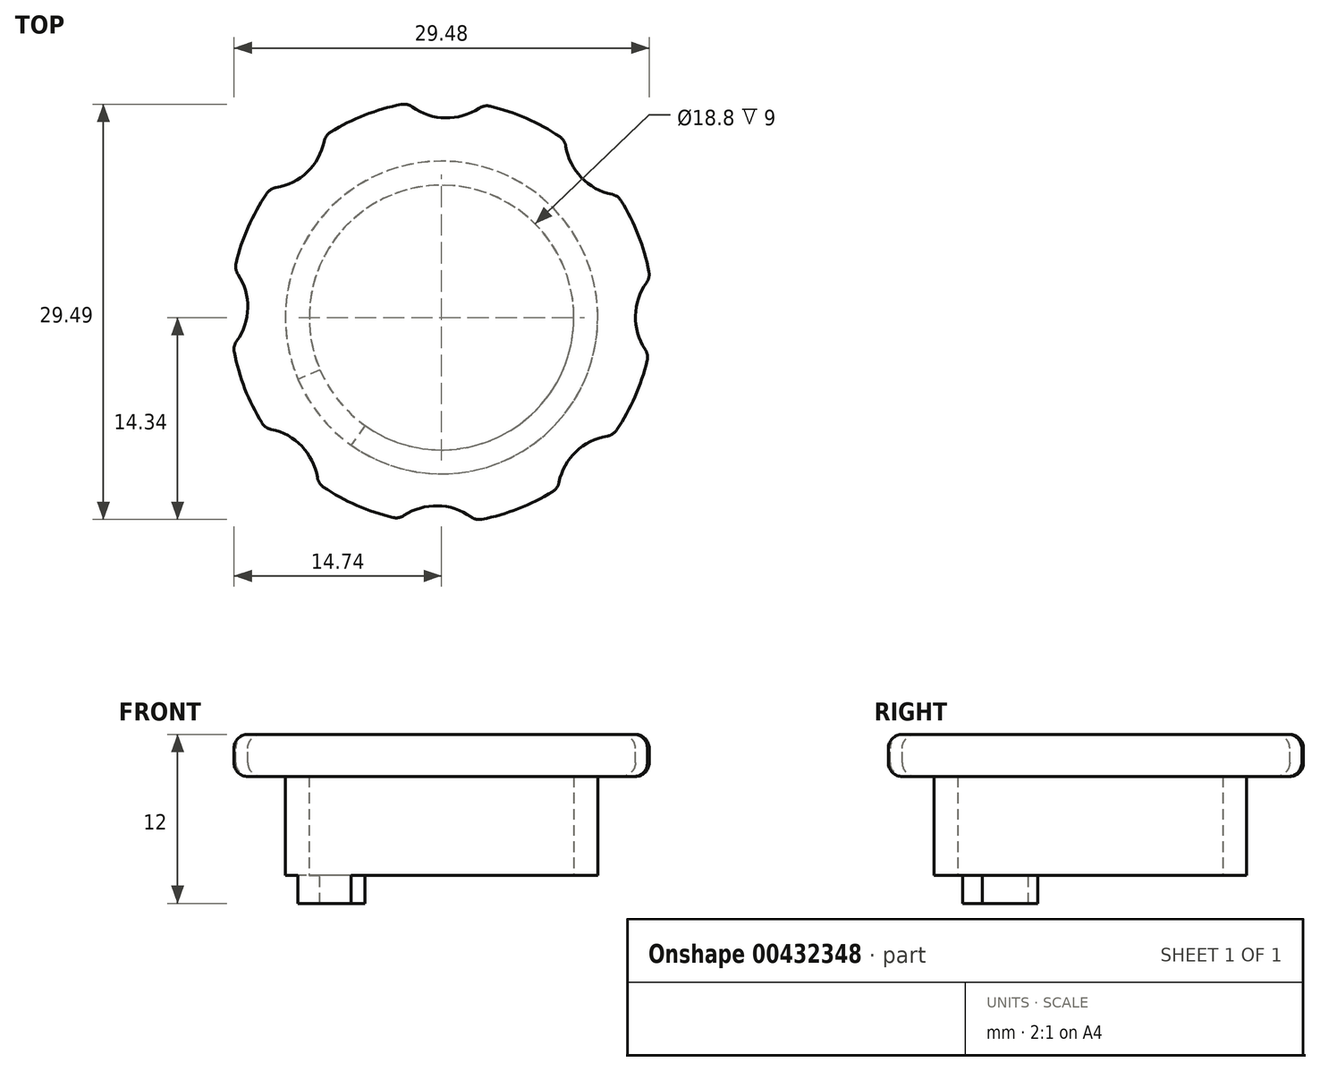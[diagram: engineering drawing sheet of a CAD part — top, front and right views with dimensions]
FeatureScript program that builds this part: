
annotation { "Feature Type Name" : "Feature", "Feature Type Description" : "" }
export const myFeature = defineFeature(function(context is Context, id is Id, definition is map)
    precondition{}
    {
        {
            var Q0;
            Q0=qCreatedBy(makeId("Top.planeOp"),FACE);
            var sketch = newSketch(context, id + "F0", { "sketchPlane" : qUnion([Q0])});
            skCircle(sketch, "E0", {"center": v(0, 0) * mm, "radius": 11.1 * mm});
            skCircle(sketch, "E1", {"center": v(0, 0) * mm, "radius": 9.4 * mm});
            skSolve(sketch);
        }
        {
            var Q0;
            Q0=makeQuery(id+"F0.imprint","IMPRINT",FACE,{"disambiguationData":[TD([[makeQuery(id+"F0.imprint","IMPRINT",EDGE,{"derivedFrom":sQuery(id+"F0.wireOp",EDGE,"E0")}),1.0]])]});
            extrude(context, id + "F1", {"entities" : qUnion([Q0]), "depth" : 10 * mm});
        }
        {
            var Q0;
            Q0=makeQuery(id+"F1.opExtrude","CAP_FACE",FACE,{"disambiguationData":[OSD([sQuery(id+"F0.wireOp",EDGE,"E0"),sQuery(id+"F0.wireOp",EDGE,"E1")])],"isStart":true});
            var sketch = newSketch(context, id + "F2", { "sketchPlane" : qUnion([Q0])});
            skLineSegment(sketch, "E2", {"start": v(-8.63, 3.72) * mm, "end": v(-10.2, 4.4) * mm});
            skLineSegment(sketch, "E3", {"start": v(-5.43, 7.67) * mm, "end": v(-6.42, 9.06) * mm});
            skArc(sketch, "E4", {"start": v(-6.42, 9.06) * mm, "mid": v(-8.63, 6.99) * mm, "end": v(-10.2, 4.4) * mm});
            skArc(sketch, "E5", {"start": v(-5.43, 7.67) * mm, "mid": v(-7.3, 5.92) * mm, "end": v(-8.63, 3.72) * mm});
            skSolve(sketch);
        }
        {
            var Q0;
            Q0=makeQuery(id+"F2.imprint","IMPRINT",FACE,{"disambiguationData":[TD([[makeQuery(id+"F2.imprint","IMPRINT",EDGE,{"derivedFrom":sQuery(id+"F2.wireOp",EDGE,"E2")}),-1.0]])]});
            extrude(context, id + "F3", {"entities" : qUnion([Q0]), "operationType" : NewBodyOperationType.ADD, "depth" : 2 * mm});
        }
        {
            var Q0;
            Q0=makeQuery(id+"F1.opExtrude","CAP_FACE",FACE,{"disambiguationData":[OSD([sQuery(id+"F0.wireOp",EDGE,"E0"),sQuery(id+"F0.wireOp",EDGE,"E1")])],"isStart":false});
            var sketch = newSketch(context, id + "F4", { "sketchPlane" : qUnion([Q0])});
            skCircle(sketch, "E6", {"center": v(0, 0.4) * mm, "radius": 15 * mm});
            skSolve(sketch);
        }
        {
            var Q0;
            Q0=makeQuery(id+"F4.imprint","IMPRINT",FACE,{"disambiguationData":[TD([[makeQuery(id+"F4.imprint","IMPRINT",EDGE,{"derivedFrom":sQuery(id+"F4.wireOp",EDGE,"E6")}),1.0]])]});
            var Q1;
            Q1=makeQuery(id+"F4.imprint","IMPRINT",FACE,{"disambiguationData":[TD([[makeQuery(id+"F4.imprint","IMPRINT",EDGE,{"derivedFrom":makeQuery(id+"F1.opExtrude","CAP_EDGE",EDGE,{"disambiguationData":[OSD([sQuery(id+"F0.wireOp",EDGE,"E0")])],"isStart":false})}),1.0]])]});
            var Q2;
            Q2=makeQuery(id+"F4.imprint","IMPRINT",FACE,{"disambiguationData":[TD([[makeQuery(id+"F4.imprint","IMPRINT",EDGE,{"derivedFrom":makeQuery(id+"F1.opExtrude","CAP_EDGE",EDGE,{"disambiguationData":[OSD([sQuery(id+"F0.wireOp",EDGE,"E1")])],"isStart":false})}),1.0]])]});
            extrude(context, id + "F5", {"entities" : qUnion([Q0, Q1, Q2]), "operationType" : NewBodyOperationType.ADD, "oppositeDirection" : true, "depth" : 3 * mm});
        }
        {
            var Q0;
            Q0=makeQuery(id+"F5.boolean.opBoolean","MERGE",FACE,{"derivedFrom":[makeQuery(id+"F1.opExtrude","CAP_FACE",FACE,{"disambiguationData":[OSD([sQuery(id+"F0.wireOp",EDGE,"E0"),sQuery(id+"F0.wireOp",EDGE,"E1")])],"isStart":false}),makeQuery(id+"F5.opExtrude","CAP_FACE",FACE,{"disambiguationData":[OSD([sQuery(id+"F4.wireOp",EDGE,"E6")])],"isStart":true})]});
            var sketch = newSketch(context, id + "F6", { "sketchPlane" : qUnion([Q0])});
            skCircle(sketch, "E7", {"center": v(0.36, 18.33) * mm, "radius": 4.17 * mm});
            skSolve(sketch);
        }
        {
            var Q0;
            {var subQ0=sQuery(id+"F6.wireOp",EDGE,"E7");var subQ1=makeQuery(id+"F5.opExtrude","CAP_EDGE",EDGE,{"disambiguationData":[OSD([sQuery(id+"F4.wireOp",EDGE,"E6")])],"isStart":true});var subQ2=makeQuery(id+"F6.imprint","INTERSECT",VERTEX,{"disambiguationData":[OD(0.0)],"derivedFrom":[subQ1,subQ0]});Q0=makeQuery(id+"F6.imprint","IMPRINT",FACE,{"disambiguationData":[TD([[makeQuery(id+"F6.imprint","IMPRINT",EDGE,{"disambiguationData":[TD([[subQ2,1.0]])],"derivedFrom":subQ0}),1.0]])]});}
            var Q1;
            {var subQ0=sQuery(id+"F6.wireOp",EDGE,"E7");var subQ1=makeQuery(id+"F5.opExtrude","CAP_EDGE",EDGE,{"disambiguationData":[OSD([sQuery(id+"F4.wireOp",EDGE,"E6")])],"isStart":true});var subQ2=makeQuery(id+"F6.imprint","INTERSECT",VERTEX,{"disambiguationData":[OD(0.0)],"derivedFrom":[subQ1,subQ0]});Q1=makeQuery(id+"F6.imprint","IMPRINT",FACE,{"disambiguationData":[TD([[makeQuery(id+"F6.imprint","IMPRINT",EDGE,{"disambiguationData":[TD([[subQ2,-1.0]])],"derivedFrom":subQ0}),1.0]])]});}
            extrude(context, id + "F7", {"entities" : qUnion([Q0, Q1]), "operationType" : NewBodyOperationType.REMOVE, "endBound" : BoundingType.THROUGH_ALL, "oppositeDirection" : true, "depth" : 25 * mm});
        }
        {
            var Q0;
            Q0=makeQuery(id+"F7.boolean.opBoolean","INTERSECT",EDGE,{"disambiguationData":[OD(0.0)],"derivedFrom":[makeQuery(id+"F5.opExtrude","SWEPT_FACE",FACE,{"disambiguationData":[OSD([sQuery(id+"F4.wireOp",EDGE,"E6")])]}),makeQuery(id+"F7.opExtrude","SWEPT_FACE",FACE,{"disambiguationData":[OSD([sQuery(id+"F6.wireOp",EDGE,"E7")])]})]});
            var Q1;
            Q1=makeQuery(id+"F7.boolean.opBoolean","COPY",EDGE,{"derivedFrom":makeQuery(id+"F7.opExtrude","CAP_EDGE",EDGE,{"disambiguationData":[OSD([sQuery(id+"F6.wireOp",EDGE,"E7")])],"isStart":true})});
            var Q2;
            {var subQ1=sQuery(id+"F4.wireOp",EDGE,"E6");Q2=makeQuery(id+"F7.boolean.opBoolean","INTERSECT",EDGE,{"derivedFrom":[makeQuery(id+"F5.boolean.opBoolean","SPLIT",FACE,{"disambiguationData":[TD([makeQuery(id+"F1.opExtrude","SWEPT_FACE",FACE,{"disambiguationData":[OSD([sQuery(id+"F0.wireOp",EDGE,"E0")])]})])],"derivedFrom":makeQuery(id+"F5.opExtrude","CAP_FACE",FACE,{"disambiguationData":[OSD([subQ1])],"isStart":false})}),makeQuery(id+"F7.opExtrude","SWEPT_FACE",FACE,{"disambiguationData":[OSD([sQuery(id+"F6.wireOp",EDGE,"E7")])]})]});}
            var Q3;
            Q3=makeQuery(id+"F7.boolean.opBoolean","INTERSECT",EDGE,{"disambiguationData":[OD(1.0)],"derivedFrom":[makeQuery(id+"F5.opExtrude","SWEPT_FACE",FACE,{"disambiguationData":[OSD([sQuery(id+"F4.wireOp",EDGE,"E6")])]}),makeQuery(id+"F7.opExtrude","SWEPT_FACE",FACE,{"disambiguationData":[OSD([sQuery(id+"F6.wireOp",EDGE,"E7")])]})]});
            fillet(context, id + "F8", {"entities" : qUnion([Q0, Q1, Q2, Q3]), "radius" : 1 * mm, "tangentPropagation" : true, "allowEdgeOverflow" : false});
        }
        {
            var Q0;
            Q0=makeQuery(id+"F1.opExtrude","SWEPT_BODY",BODY,{"disambiguationData":[OSD([sQuery(id+"F0.wireOp",EDGE,"E0"),sQuery(id+"F0.wireOp",EDGE,"E1")])]});
            var Q1;
            {var subQ0=sQuery(id+"F6.wireOp",EDGE,"E7");var subQ1=sQuery(id+"F4.wireOp",EDGE,"E6");Q1=makeQuery(id+"F8.opFillet","BLEND_FACE",FACE,{"disambiguationData":[OSD([subQ1,subQ0]),TDD([makeQuery(id+"F7.boolean.opBoolean","INTERSECT",EDGE,{"disambiguationData":[OD(0.0)],"derivedFrom":[makeQuery(id+"F5.opExtrude","SWEPT_FACE",FACE,{"disambiguationData":[OSD([subQ1])]}),makeQuery(id+"F7.opExtrude","SWEPT_FACE",FACE,{"disambiguationData":[OSD([subQ0])]})]})])]});}
            var Q2;
            Q2=makeQuery(id+"F8.opFillet","BLEND_FACE",FACE,{"disambiguationData":[OSD([sQuery(id+"F6.wireOp",EDGE,"E7")])]});
            var Q3;
            Q3=makeQuery(id+"F7.boolean.opBoolean","COPY",FACE,{"derivedFrom":makeQuery(id+"F7.opExtrude","SWEPT_FACE",FACE,{"disambiguationData":[OSD([sQuery(id+"F6.wireOp",EDGE,"E7")])]})});
            var Q4;
            {var subQ0=sQuery(id+"F6.wireOp",EDGE,"E7");var subQ1=sQuery(id+"F4.wireOp",EDGE,"E6");Q4=makeQuery(id+"F8.opFillet","BLEND_FACE",FACE,{"disambiguationData":[OSD([subQ1,subQ0]),TDD([makeQuery(id+"F7.boolean.opBoolean","INTERSECT",EDGE,{"disambiguationData":[OD(1.0)],"derivedFrom":[makeQuery(id+"F5.opExtrude","SWEPT_FACE",FACE,{"disambiguationData":[OSD([subQ1])]}),makeQuery(id+"F7.opExtrude","SWEPT_FACE",FACE,{"disambiguationData":[OSD([subQ0])]})]})])]});}
            var Q5;
            {var subQ0=sQuery(id+"F6.wireOp",EDGE,"E7");var subQ2=sQuery(id+"F4.wireOp",EDGE,"E6");Q5=makeQuery(id+"F8.opFillet","BLEND_FACE",FACE,{"disambiguationData":[OSD([subQ2,subQ0]),TDD([makeQuery(id+"F7.boolean.opBoolean","INTERSECT",EDGE,{"derivedFrom":[makeQuery(id+"F5.boolean.opBoolean","SPLIT",FACE,{"disambiguationData":[TD([makeQuery(id+"F1.opExtrude","SWEPT_FACE",FACE,{"disambiguationData":[OSD([sQuery(id+"F0.wireOp",EDGE,"E0")])]})])],"derivedFrom":makeQuery(id+"F5.opExtrude","CAP_FACE",FACE,{"disambiguationData":[OSD([subQ2])],"isStart":false})}),makeQuery(id+"F7.opExtrude","SWEPT_FACE",FACE,{"disambiguationData":[OSD([subQ0])]})]})])]});}
            var Q6;
            Q6=makeQuery(id+"F5.opExtrude","SWEPT_FACE",FACE,{"disambiguationData":[OSD([sQuery(id+"F4.wireOp",EDGE,"E6")])]});
            circularPattern(context, id + "F9", {"patternType" : PatternType.FACE, "faces" : qUnion([Q1, Q2, Q3, Q4, Q5]), "axis" : qUnion([Q6]), "angle" : 360 * degree, "instanceCount" : 8, "equalSpace" : true});
        }
        {
            var Q0;
            Q0=makeQuery(id+"F9.opPattern","SPLIT",EDGE,{"disambiguationData":[OD(4.0)],"derivedFrom":makeQuery(id+"F5.opExtrude","CAP_EDGE",EDGE,{"disambiguationData":[OSD([sQuery(id+"F4.wireOp",EDGE,"E6")])],"isStart":false})});
            var Q1;
            Q1=makeQuery(id+"F9.opPattern","SPLIT",EDGE,{"disambiguationData":[OD(5.0)],"derivedFrom":makeQuery(id+"F5.opExtrude","CAP_EDGE",EDGE,{"disambiguationData":[OSD([sQuery(id+"F4.wireOp",EDGE,"E6")])],"isStart":false})});
            var Q2;
            Q2=makeQuery(id+"F9.opPattern","SPLIT",EDGE,{"disambiguationData":[OD(3.0)],"derivedFrom":makeQuery(id+"F5.opExtrude","CAP_EDGE",EDGE,{"disambiguationData":[OSD([sQuery(id+"F4.wireOp",EDGE,"E6")])],"isStart":true})});
            var Q3;
            Q3=makeQuery(id+"F9.opPattern","SPLIT",EDGE,{"disambiguationData":[OD(2.0)],"derivedFrom":makeQuery(id+"F5.opExtrude","CAP_EDGE",EDGE,{"disambiguationData":[OSD([sQuery(id+"F4.wireOp",EDGE,"E6")])],"isStart":false})});
            var Q4;
            Q4=makeQuery(id+"F9.opPattern","SPLIT",EDGE,{"disambiguationData":[OD(3.0)],"derivedFrom":makeQuery(id+"F5.opExtrude","CAP_EDGE",EDGE,{"disambiguationData":[OSD([sQuery(id+"F4.wireOp",EDGE,"E6")])],"isStart":false})});
            var Q5;
            Q5=makeQuery(id+"F9.opPattern","SPLIT",EDGE,{"disambiguationData":[OD(0.0)],"derivedFrom":makeQuery(id+"F5.opExtrude","CAP_EDGE",EDGE,{"disambiguationData":[OSD([sQuery(id+"F4.wireOp",EDGE,"E6")])],"isStart":false})});
            var Q6;
            Q6=makeQuery(id+"F9.opPattern","SPLIT",EDGE,{"disambiguationData":[OD(1.0)],"derivedFrom":makeQuery(id+"F5.opExtrude","CAP_EDGE",EDGE,{"disambiguationData":[OSD([sQuery(id+"F4.wireOp",EDGE,"E6")])],"isStart":false})});
            var Q7;
            Q7=makeQuery(id+"F9.opPattern","SPLIT",EDGE,{"disambiguationData":[OD(7.0)],"derivedFrom":makeQuery(id+"F5.opExtrude","CAP_EDGE",EDGE,{"disambiguationData":[OSD([sQuery(id+"F4.wireOp",EDGE,"E6")])],"isStart":false})});
            var Q8;
            Q8=makeQuery(id+"F9.opPattern","SPLIT",EDGE,{"disambiguationData":[OD(6.0)],"derivedFrom":makeQuery(id+"F5.opExtrude","CAP_EDGE",EDGE,{"disambiguationData":[OSD([sQuery(id+"F4.wireOp",EDGE,"E6")])],"isStart":false})});
            var Q9;
            Q9=makeQuery(id+"F9.opPattern","SPLIT",EDGE,{"disambiguationData":[OD(4.0)],"derivedFrom":makeQuery(id+"F5.opExtrude","CAP_EDGE",EDGE,{"disambiguationData":[OSD([sQuery(id+"F4.wireOp",EDGE,"E6")])],"isStart":true})});
            var Q10;
            Q10=makeQuery(id+"F9.opPattern","SPLIT",EDGE,{"disambiguationData":[OD(5.0)],"derivedFrom":makeQuery(id+"F5.opExtrude","CAP_EDGE",EDGE,{"disambiguationData":[OSD([sQuery(id+"F4.wireOp",EDGE,"E6")])],"isStart":true})});
            var Q11;
            Q11=makeQuery(id+"F9.opPattern","SPLIT",EDGE,{"disambiguationData":[OD(6.0)],"derivedFrom":makeQuery(id+"F5.opExtrude","CAP_EDGE",EDGE,{"disambiguationData":[OSD([sQuery(id+"F4.wireOp",EDGE,"E6")])],"isStart":true})});
            var Q12;
            Q12=makeQuery(id+"F9.opPattern","SPLIT",EDGE,{"disambiguationData":[OD(7.0)],"derivedFrom":makeQuery(id+"F5.opExtrude","CAP_EDGE",EDGE,{"disambiguationData":[OSD([sQuery(id+"F4.wireOp",EDGE,"E6")])],"isStart":true})});
            var Q13;
            Q13=makeQuery(id+"F9.opPattern","SPLIT",EDGE,{"disambiguationData":[OD(1.0)],"derivedFrom":makeQuery(id+"F5.opExtrude","CAP_EDGE",EDGE,{"disambiguationData":[OSD([sQuery(id+"F4.wireOp",EDGE,"E6")])],"isStart":true})});
            var Q14;
            Q14=makeQuery(id+"F9.opPattern","SPLIT",EDGE,{"disambiguationData":[OD(0.0)],"derivedFrom":makeQuery(id+"F5.opExtrude","CAP_EDGE",EDGE,{"disambiguationData":[OSD([sQuery(id+"F4.wireOp",EDGE,"E6")])],"isStart":true})});
            var Q15;
            Q15=makeQuery(id+"F9.opPattern","SPLIT",EDGE,{"disambiguationData":[OD(2.0)],"derivedFrom":makeQuery(id+"F5.opExtrude","CAP_EDGE",EDGE,{"disambiguationData":[OSD([sQuery(id+"F4.wireOp",EDGE,"E6")])],"isStart":true})});
            fillet(context, id + "F10", {"entities" : qUnion([Q0, Q1, Q2, Q3, Q4, Q5, Q6, Q7, Q8, Q9, Q10, Q11, Q12, Q13, Q14, Q15]), "radius" : 1 * mm, "tangentPropagation" : true, "allowEdgeOverflow" : false});
        }
    });
